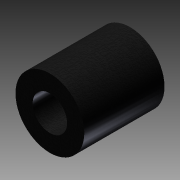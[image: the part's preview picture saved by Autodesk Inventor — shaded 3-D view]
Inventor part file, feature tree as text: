
AUTODESK INVENTOR PART (.ipt)
format: ipt  version: 2011 SP1 (Build 150282100, 282)  size: 81,920 bytes
history: native  units: in
note: dims shown in document units (in); Inventor stores cm internally (conversion verified against a paired STEP export)
features: extrude x1, sketch x1
ambient origin geometry x8: Origin, YZ Plane, XZ Plane, XY Plane, X Axis, Y Axis, Z Axis, Center Point
bodies: Solid1 (feature_tree)
feature tree (2):
  extrude  "Extrusion1"  Depth=1.5in
  sketch  "Sketch1"  dims[d0=0.375in d1=1.5in d2=1.75in d3=0.0in]
